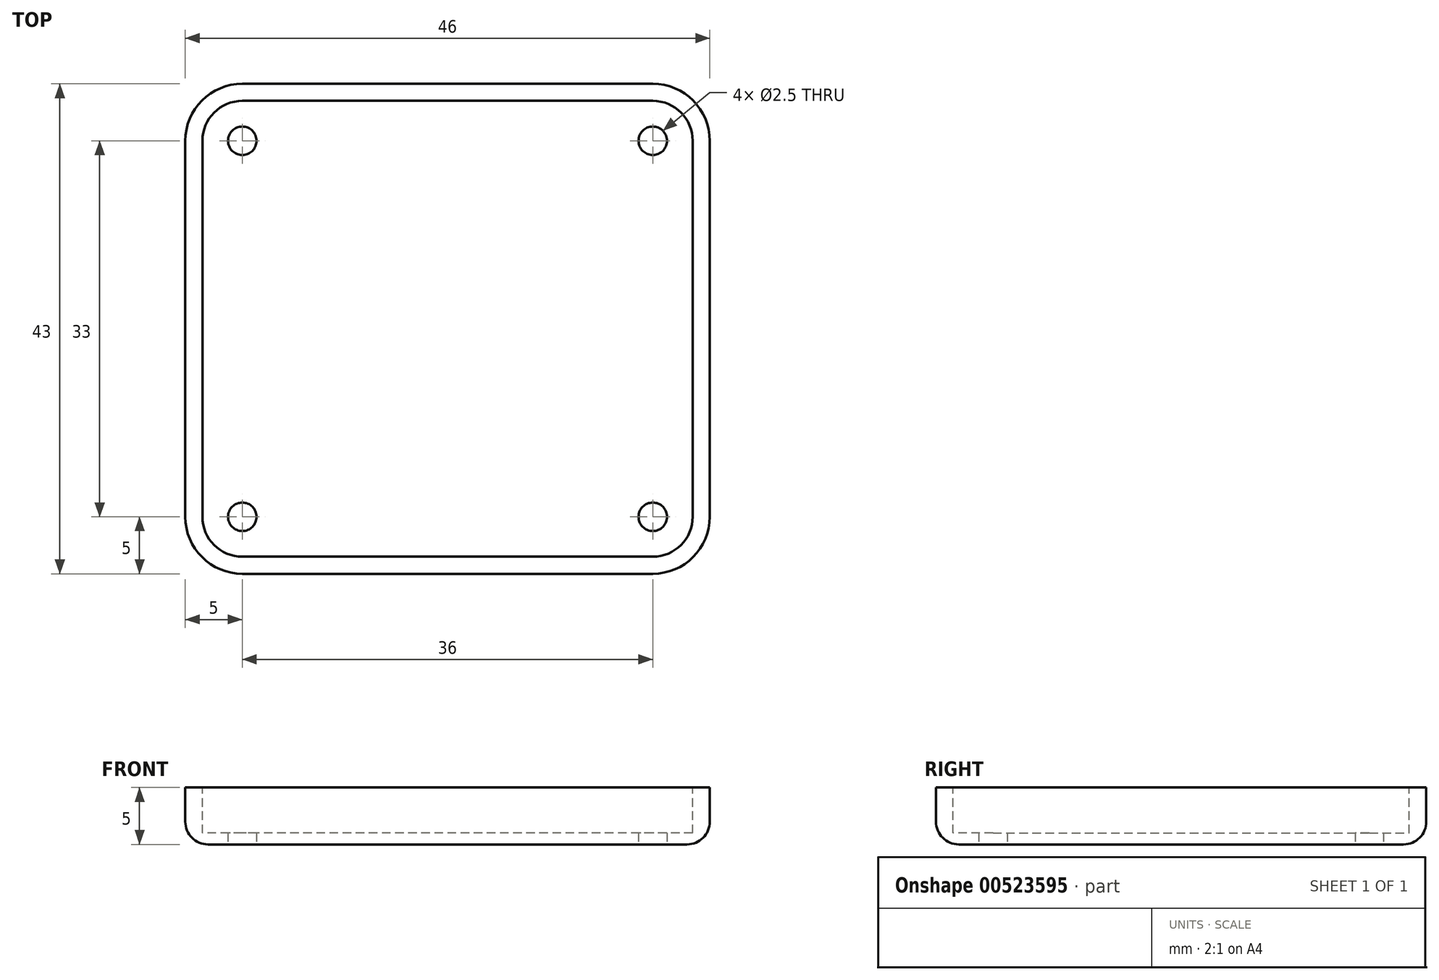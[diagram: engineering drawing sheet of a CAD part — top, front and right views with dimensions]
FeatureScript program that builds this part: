
annotation { "Feature Type Name" : "Feature", "Feature Type Description" : "" }
export const myFeature = defineFeature(function(context is Context, id is Id, definition is map)
    precondition{}
    {
        {
            var Q0;
            Q0=qCreatedBy(makeId("Top.planeOp"),FACE);
            var sketch = newSketch(context, id + "F0", { "sketchPlane" : qUnion([Q0])});
            skLineSegment(sketch, "E0.bottom", {"start": v(18, -21.5) * mm, "end": v(-18, -21.5) * mm});
            skLineSegment(sketch, "E0.top", {"start": v(18, 21.5) * mm, "end": v(-18, 21.5) * mm});
            skLineSegment(sketch, "E0.left", {"start": v(23, -16.5) * mm, "end": v(23, 16.5) * mm});
            skLineSegment(sketch, "E0.right", {"start": v(-23, -16.5) * mm, "end": v(-23, 16.5) * mm});
            skPoint(sketch, "E0.middle", {"position": v(0, 0) * mm});
            skPoint(sketch, "E1.visualSharp", {"position": v(-23, 21.5) * mm});
            skArc(sketch, "E1.filletArc", {"start": v(-18, 21.5) * mm, "mid": v(-21.54, 20.04) * mm, "end": v(-23, 16.5) * mm});
            skPoint(sketch, "E2.visualSharp", {"position": v(23, 21.5) * mm});
            skArc(sketch, "E2.filletArc", {"start": v(23, 16.5) * mm, "mid": v(21.54, 20.04) * mm, "end": v(18, 21.5) * mm});
            skPoint(sketch, "E3.visualSharp", {"position": v(23, -21.5) * mm});
            skArc(sketch, "E3.filletArc", {"start": v(18, -21.5) * mm, "mid": v(21.54, -20.04) * mm, "end": v(23, -16.5) * mm});
            skPoint(sketch, "E4.visualSharp", {"position": v(-23, -21.5) * mm});
            skArc(sketch, "E4.filletArc", {"start": v(-23, -16.5) * mm, "mid": v(-21.54, -20.04) * mm, "end": v(-18, -21.5) * mm});
            skSolve(sketch);
        }
        {
            var Q0;
            Q0 = qSketchRegion(id + "F0", true);
            extrude(context, id + "F1", {"entities" : qUnion([Q0]), "depth" : 5 * mm, "offsetDistance" : 25 * mm});
        }
        {
            var Q0;
            Q0=makeQuery(id+"F1.opExtrude","CAP_FACE",FACE,{"disambiguationData":[OSD([sQuery(id+"F0.wireOp",EDGE,"E0.bottom"),sQuery(id+"F0.wireOp",EDGE,"E0.top"),sQuery(id+"F0.wireOp",EDGE,"E0.left"),sQuery(id+"F0.wireOp",EDGE,"E0.right"),sQuery(id+"F0.wireOp",EDGE,"E1.filletArc"),sQuery(id+"F0.wireOp",EDGE,"E2.filletArc"),sQuery(id+"F0.wireOp",EDGE,"E3.filletArc"),sQuery(id+"F0.wireOp",EDGE,"E4.filletArc")])],"isStart":false});
            var sketch = newSketch(context, id + "F2", { "sketchPlane" : qUnion([Q0])});
            skLineSegment(sketch, "E5.bottom", {"start": v(18, -20) * mm, "end": v(-18, -20) * mm});
            skLineSegment(sketch, "E5.top", {"start": v(18, 20) * mm, "end": v(-18, 20) * mm});
            skLineSegment(sketch, "E5.left", {"start": v(21.5, -16.5) * mm, "end": v(21.5, 16.5) * mm});
            skLineSegment(sketch, "E5.right", {"start": v(-21.5, -16.5) * mm, "end": v(-21.5, 16.5) * mm});
            skPoint(sketch, "E5.middle", {"position": v(0, 0) * mm});
            skPoint(sketch, "E6.visualSharp", {"position": v(-21.5, 20) * mm});
            skArc(sketch, "E6.filletArc", {"start": v(-18, 20) * mm, "mid": v(-20.47, 18.97) * mm, "end": v(-21.5, 16.5) * mm});
            skPoint(sketch, "E7.visualSharp", {"position": v(21.5, 20) * mm});
            skArc(sketch, "E7.filletArc", {"start": v(21.5, 16.5) * mm, "mid": v(20.47, 18.97) * mm, "end": v(18, 20) * mm});
            skPoint(sketch, "E8.visualSharp", {"position": v(21.5, -20) * mm});
            skArc(sketch, "E8.filletArc", {"start": v(18, -20) * mm, "mid": v(20.47, -18.97) * mm, "end": v(21.5, -16.5) * mm});
            skPoint(sketch, "E9.visualSharp", {"position": v(-21.5, -20) * mm});
            skArc(sketch, "E9.filletArc", {"start": v(-21.5, -16.5) * mm, "mid": v(-20.47, -18.97) * mm, "end": v(-18, -20) * mm});
            skSolve(sketch);
        }
        {
            var Q0;
            Q0=makeQuery(id+"F2.imprint","IMPRINT",FACE,{"disambiguationData":[TD([[makeQuery(id+"F2.imprint","IMPRINT",EDGE,{"derivedFrom":sQuery(id+"F2.wireOp",EDGE,"E5.bottom")}),-1.0]])]});
            extrude(context, id + "F3", {"entities" : qUnion([Q0]), "operationType" : NewBodyOperationType.REMOVE, "oppositeDirection" : true, "depth" : 4 * mm, "offsetDistance" : 25 * mm});
        }
        {
            var Q0;
            Q0=makeQuery(id+"F1.opExtrude","CAP_FACE",FACE,{"disambiguationData":[OSD([sQuery(id+"F0.wireOp",EDGE,"E0.bottom"),sQuery(id+"F0.wireOp",EDGE,"E0.top"),sQuery(id+"F0.wireOp",EDGE,"E0.left"),sQuery(id+"F0.wireOp",EDGE,"E0.right"),sQuery(id+"F0.wireOp",EDGE,"E1.filletArc"),sQuery(id+"F0.wireOp",EDGE,"E2.filletArc"),sQuery(id+"F0.wireOp",EDGE,"E3.filletArc"),sQuery(id+"F0.wireOp",EDGE,"E4.filletArc")])],"isStart":true});
            fillet(context, id + "F4", {"entities" : qUnion([Q0]), "radius" : 2 * mm, "tangentPropagation" : true, "allowEdgeOverflow" : false});
        }
        {
            var Q0;
            Q0=makeQuery(id+"F1.opExtrude","CAP_FACE",FACE,{"disambiguationData":[OSD([sQuery(id+"F0.wireOp",EDGE,"E0.bottom"),sQuery(id+"F0.wireOp",EDGE,"E0.top"),sQuery(id+"F0.wireOp",EDGE,"E0.left"),sQuery(id+"F0.wireOp",EDGE,"E0.right"),sQuery(id+"F0.wireOp",EDGE,"E1.filletArc"),sQuery(id+"F0.wireOp",EDGE,"E2.filletArc"),sQuery(id+"F0.wireOp",EDGE,"E3.filletArc"),sQuery(id+"F0.wireOp",EDGE,"E4.filletArc")])],"isStart":true});
            var sketch = newSketch(context, id + "F5", { "sketchPlane" : qUnion([Q0])});
            skLineSegment(sketch, "E10.bottom", {"start": v(18, -16.5) * mm, "end": v(-18, -16.5) * mm, "construction": true});
            skLineSegment(sketch, "E10.top", {"start": v(18, 16.5) * mm, "end": v(-18, 16.5) * mm, "construction": true});
            skLineSegment(sketch, "E10.left", {"start": v(18, -16.5) * mm, "end": v(18, 16.5) * mm, "construction": true});
            skLineSegment(sketch, "E10.right", {"start": v(-18, -16.5) * mm, "end": v(-18, 16.5) * mm, "construction": true});
            skPoint(sketch, "E10.middle", {"position": v(0, 0) * mm});
            skCircle(sketch, "E11", {"center": v(-18, 16.5) * mm, "radius": 1.25 * mm});
            skCircle(sketch, "E12", {"center": v(18, 16.5) * mm, "radius": 1.25 * mm});
            skCircle(sketch, "E13", {"center": v(18, -16.5) * mm, "radius": 1.25 * mm});
            skCircle(sketch, "E14", {"center": v(-18, -16.5) * mm, "radius": 1.25 * mm});
            skSolve(sketch);
        }
        {
            var Q0;
            Q0=makeQuery(id+"F5.imprint","IMPRINT",FACE,{"disambiguationData":[TD([[makeQuery(id+"F5.imprint","IMPRINT",EDGE,{"derivedFrom":sQuery(id+"F5.wireOp",EDGE,"E11")}),1.0]])]});
            var Q1;
            Q1=makeQuery(id+"F5.imprint","IMPRINT",FACE,{"disambiguationData":[TD([[makeQuery(id+"F5.imprint","IMPRINT",EDGE,{"derivedFrom":sQuery(id+"F5.wireOp",EDGE,"E12")}),1.0]])]});
            var Q2;
            Q2=makeQuery(id+"F5.imprint","IMPRINT",FACE,{"disambiguationData":[TD([[makeQuery(id+"F5.imprint","IMPRINT",EDGE,{"derivedFrom":sQuery(id+"F5.wireOp",EDGE,"E13")}),1.0]])]});
            var Q3;
            Q3=makeQuery(id+"F5.imprint","IMPRINT",FACE,{"disambiguationData":[TD([[makeQuery(id+"F5.imprint","IMPRINT",EDGE,{"derivedFrom":sQuery(id+"F5.wireOp",EDGE,"E14")}),1.0]])]});
            var Q4;
            Q4=sQuery(id+"F5.wireOp",EDGE,"E11");
            extrude(context, id + "F6", {"entities" : qUnion([Q0, Q1, Q2, Q3]), "operationType" : NewBodyOperationType.REMOVE, "surfaceEntities" : qUnion([Q4]), "endBound" : BoundingType.THROUGH_ALL, "oppositeDirection" : true, "depth" : 9.1 * mm, "offsetDistance" : 25 * mm});
        }
    });
